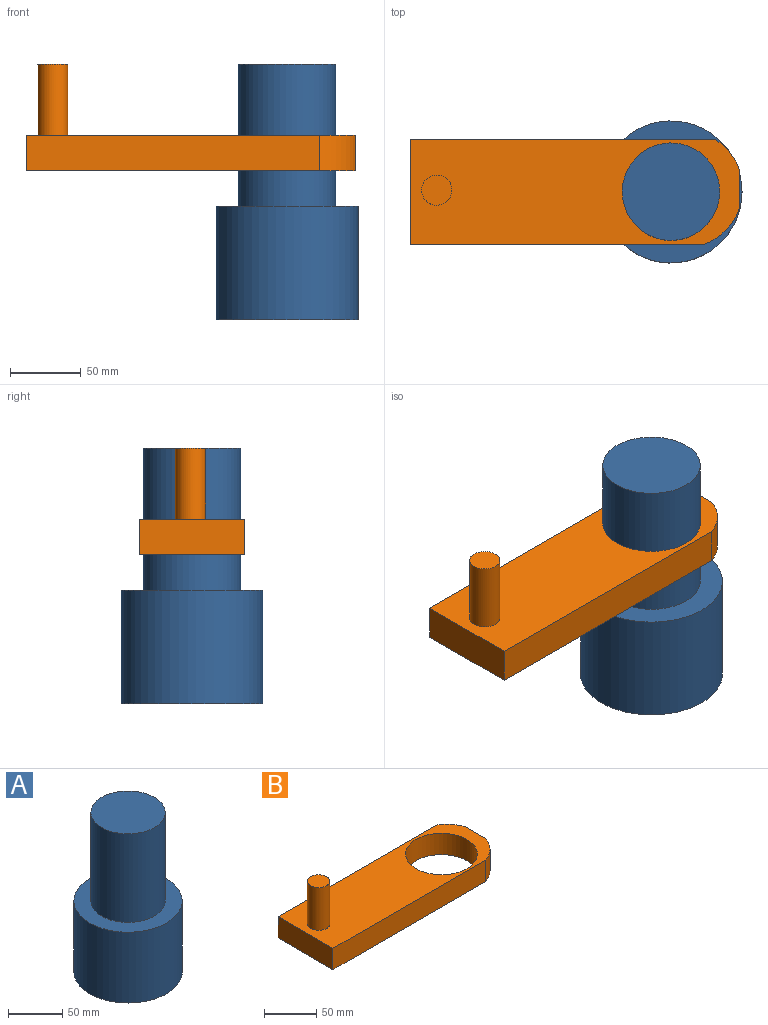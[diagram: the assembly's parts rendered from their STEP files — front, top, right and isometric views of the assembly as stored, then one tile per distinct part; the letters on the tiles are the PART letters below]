
ASSEMBLY  parts=2 mates=1
PART A: 5 faces, bbox 100x100x180 mm
  f0: cylinder r=50mm len=100mm, axis (0,0,-1), area 25132.7mm2, adj f1,f2
  f1: plane 100x100mm, normal (0,0,1), area 4152.6mm2, adj f0,f3
  f2: plane 100x100mm, normal (0,0,-1), area 7854mm2, adj f0
  f3: cylinder r=34.32mm len=100mm, axis (0,0,-1), area 21566.9mm2, adj f1,f4
  f4: plane 68.65x68.65mm, normal (0,0,1), area 3701.4mm2, adj f3
PART B: 13 faces, bbox 232x74.3x75 mm
  f0: plane 27.69x25mm, normal (1,0,0), area 665mm2, adj f1,f6,f7,f8,f9
  f1: cylinder r=41.32mm len=25mm, axis (0,0,-1), area 703.9mm2, adj f0,f2,f7,f8
  f2: plane 214.58x25mm, normal (0,1,0), area 5364.4mm2, adj f1,f3,f7,f8
  f3: plane 74.33x25mm, normal (-1,0,0), area 1858.3mm2, adj f2,f4,f7,f8
  f4: plane 206.56x25mm, normal (0,-1,0), area 5164mm2, adj f3,f6,f7,f8
  f5: cylinder r=34.32mm len=68.65mm, axis (0,0,-1), area 5391.7mm2, adj f7,f8
  f6: cylinder r=41.32mm len=25.43mm, axis (0,0,-1), area 925.9mm2, adj f0,f4,f7,f8
  f7: plane 231.99x74.33mm, normal (0,0,1), area 12822.8mm2, adj f0,f1,f2,f3,f4,f5,f6,f11
  f8: plane 231.99x74.33mm, normal (0,0,-1), area 13178mm2, adj f0,f1,f2,f3,f4,f5,f6
  f9: cylinder r=2.95mm len=5.89mm, axis (1,0,0), area 46.3mm2, adj f0,f10
  f10: plane 5.89x5.89mm, normal (1,0,0), area 27.3mm2, adj f9
  f11: cylinder r=10.63mm len=50mm, axis (0,0,-1), area 3340.4mm2, adj f7,f12
  f12: plane 21.27x21.27mm, normal (0,0,1), area 355.2mm2, adj f11
PLACE A t=(98.81,37.78,3.84)mm
PLACE B t=(98.81,37.78,-71.16)mm
MATE fastened A.f0 <-> B.f5  axis (0,0,-1) through (52.58,68.57,133.84)mm
